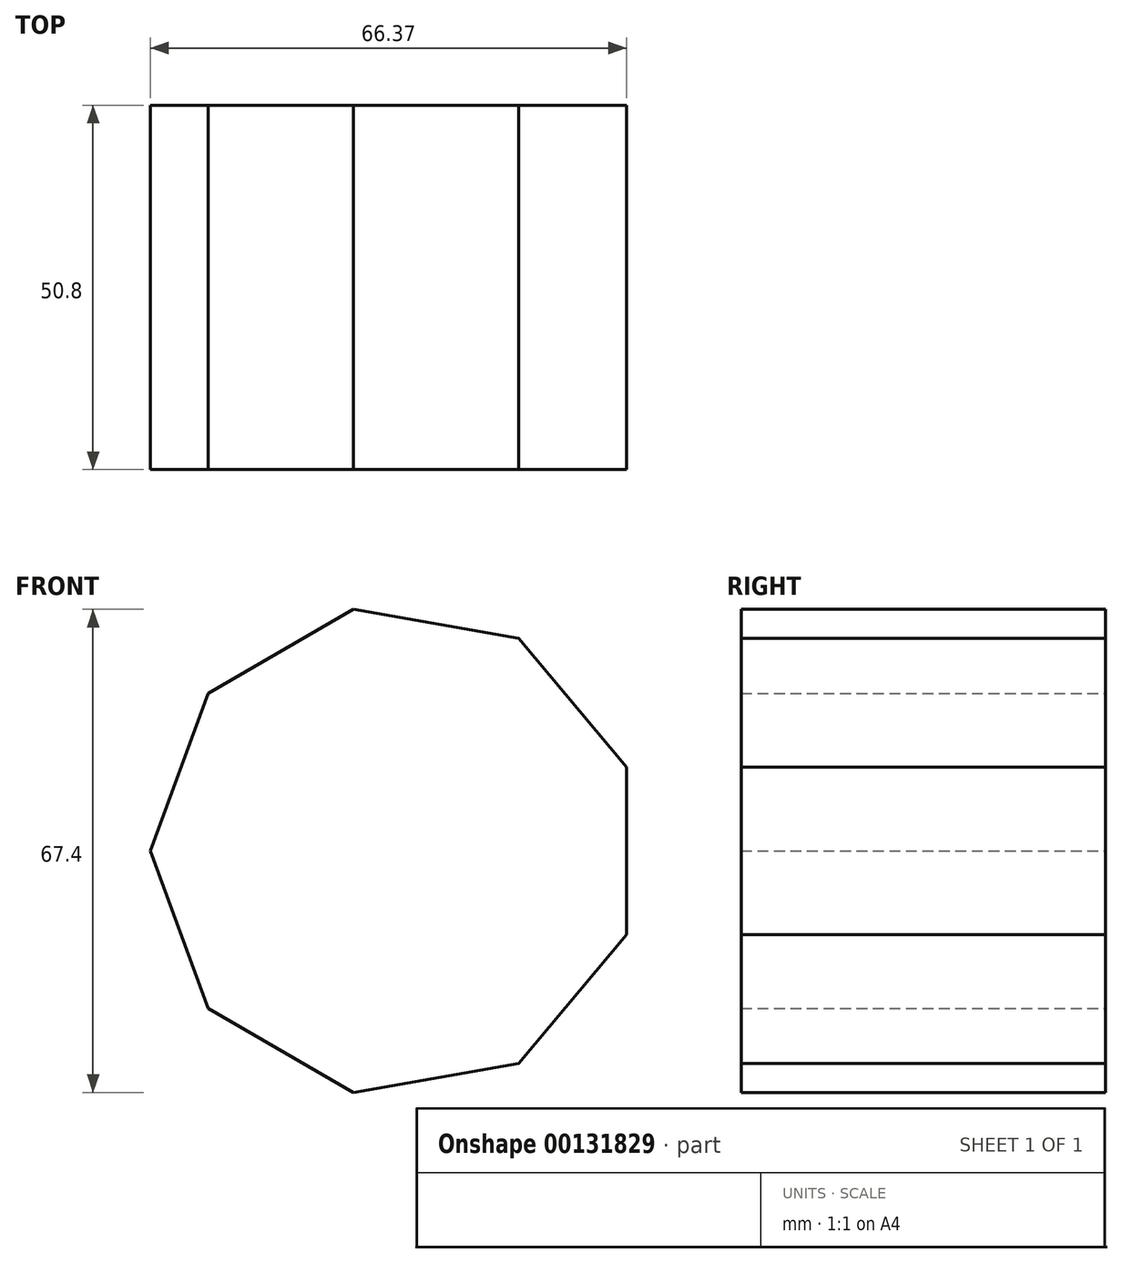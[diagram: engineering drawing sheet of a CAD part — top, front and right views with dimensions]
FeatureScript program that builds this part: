
annotation { "Feature Type Name" : "Feature", "Feature Type Description" : "" }
export const myFeature = defineFeature(function(context is Context, id is Id, definition is map)
    precondition{}
    {
        {
            var Q0;
            Q0=qCreatedBy(makeId("Front.planeOp"),FACE);
            var sketch = newSketch(context, id + "F0", { "sketchPlane" : qUnion([Q0])});
            skCircle(sketch, "E0.cCircle", {"center": v(0, 0) * mm, "radius": 32.15 * mm, "construction": true});
            skLineSegment(sketch, "E0.0", {"start": v(32.15, 11.7) * mm, "end": v(32.15, -11.7) * mm});
            skLineSegment(sketch, "E0.1", {"start": v(32.15, -11.7) * mm, "end": v(17.1, -29.63) * mm});
            skLineSegment(sketch, "E0.2", {"start": v(17.1, -29.63) * mm, "end": v(-5.94, -33.7) * mm});
            skLineSegment(sketch, "E0.3", {"start": v(-5.94, -33.7) * mm, "end": v(-26.21, -22) * mm});
            skLineSegment(sketch, "E0.4", {"start": v(-26.21, -22) * mm, "end": v(-34.22, 0) * mm});
            skLineSegment(sketch, "E0.5", {"start": v(-34.22, 0) * mm, "end": v(-26.21, 22) * mm});
            skLineSegment(sketch, "E0.6", {"start": v(-26.21, 22) * mm, "end": v(-5.94, 33.7) * mm});
            skLineSegment(sketch, "E0.7", {"start": v(-5.94, 33.7) * mm, "end": v(17.1, 29.63) * mm});
            skLineSegment(sketch, "E0.8", {"start": v(17.1, 29.63) * mm, "end": v(32.15, 11.7) * mm});
            skPoint(sketch, "E0.0.midPoint", {"position": v(32.15, 0) * mm});
            skSolve(sketch);
        }
        {
            var Q0;
            Q0 = qSketchRegion(id + "F0", true);
            extrude(context, id + "F1", {"entities" : qUnion([Q0]), "endBound" : BoundingType.SYMMETRIC, "depth" : 50.8 * mm});
        }
    });
